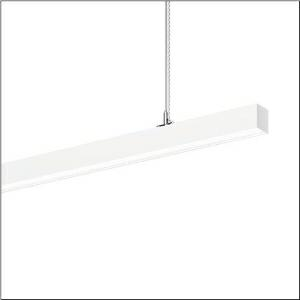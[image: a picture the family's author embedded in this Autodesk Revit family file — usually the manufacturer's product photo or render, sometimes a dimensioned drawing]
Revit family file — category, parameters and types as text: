
# Revit family: silica_r__21_51mx30dc49wb_27b8
name_source: partatom
category: Lighting Fixtures
units: mm (PartAtom-declared; Revit-internal decimal feet)

## family parameters
Cut with Voids When Loaded = No
Host = Face
Light Source = No
Part Type = Normal
Room Calculation Point = No
Round Connector Dimension = Use Diameter
Shared = No

## types (1)
- --- (1 x LED, 10520 lm, 64.1 W, 4000K)
    Apparent Load = 64 VA
    CIE Flux Codes = 47 79 96 57 100
    Color Rendering = 80
    Color Temperature = 4000K
    Default Elevation = 1800 mm
    Description = Silica® 21, office luminaire, primary optical cover: cover, of PMMA, opal, light emission: direct/indirect distribution, primary light characteristic: symmetric, installation type: suspended mounting, LED, rated luminous flux: 10.520lm, luminous efficacy: 164lm/W, light colour: 840, colour temperature: 4000K, with terminal, 3+2-pole, max. 2.5mm², mains connection: 220..240V, AC, 50/60Hz, rated input power: 64.1W, luminaire housing, of aluminium, traffic white (RAL 9016), length: 3.004mm, width: 53mm, height: 53mm, protection rating (complete): IP20, insulation class (complete): insulation class I (protective earthing), certification: CE, permissible operating ambient temperature: 0..+35°C, standard: EN 50419, packaging unit: 1 piece
    Height = 53 mm
    Lamp = 1 x LED
    Lamp Light Flux = 10520 lm
    Lamp Power = 64.1 W
    Lamp count = 1
    Length = 3004 mm
    Luminous efficacy = 164 lm/W
    Manufacturer = Siteco
    ModVariant = No
    Model = 51MX30DC49WB
    Mounting Place = Ceiling
    Mounting Type = Pendant
    Number of Poles = 1
    OnlyDefault = Yes
    Power Factor = 1
    Product Name = Silica® 21
    Product group = office luminaire | ceiling pendant
    ProductGroupID = 905
    Protection Class = Protection class I
    Protection Degree = IP 20
    RLX_Detail_Level = 1
    RlxData = <blob elided: 21301 chars, md5=77ca7a1d>
    Socket = socket
    Standby Power = 0 W
    System Light Flux = 10520 lm
    System Power = 64 W
    Type Comments = factory setting: luminous flux: 100 % | dim-lin: 254 | 218 mA
    Type Image = l_1251642.jpg
    URL = http://relux.com
    VarID = @adj_025835
    Voltage = 0 V
    Weight = 0.00 kg
    Width = 53 mm

## geometry (parser evidence)
native form markers: Blend x4, Sweep x14
no freeform markers — native parametric forms only
